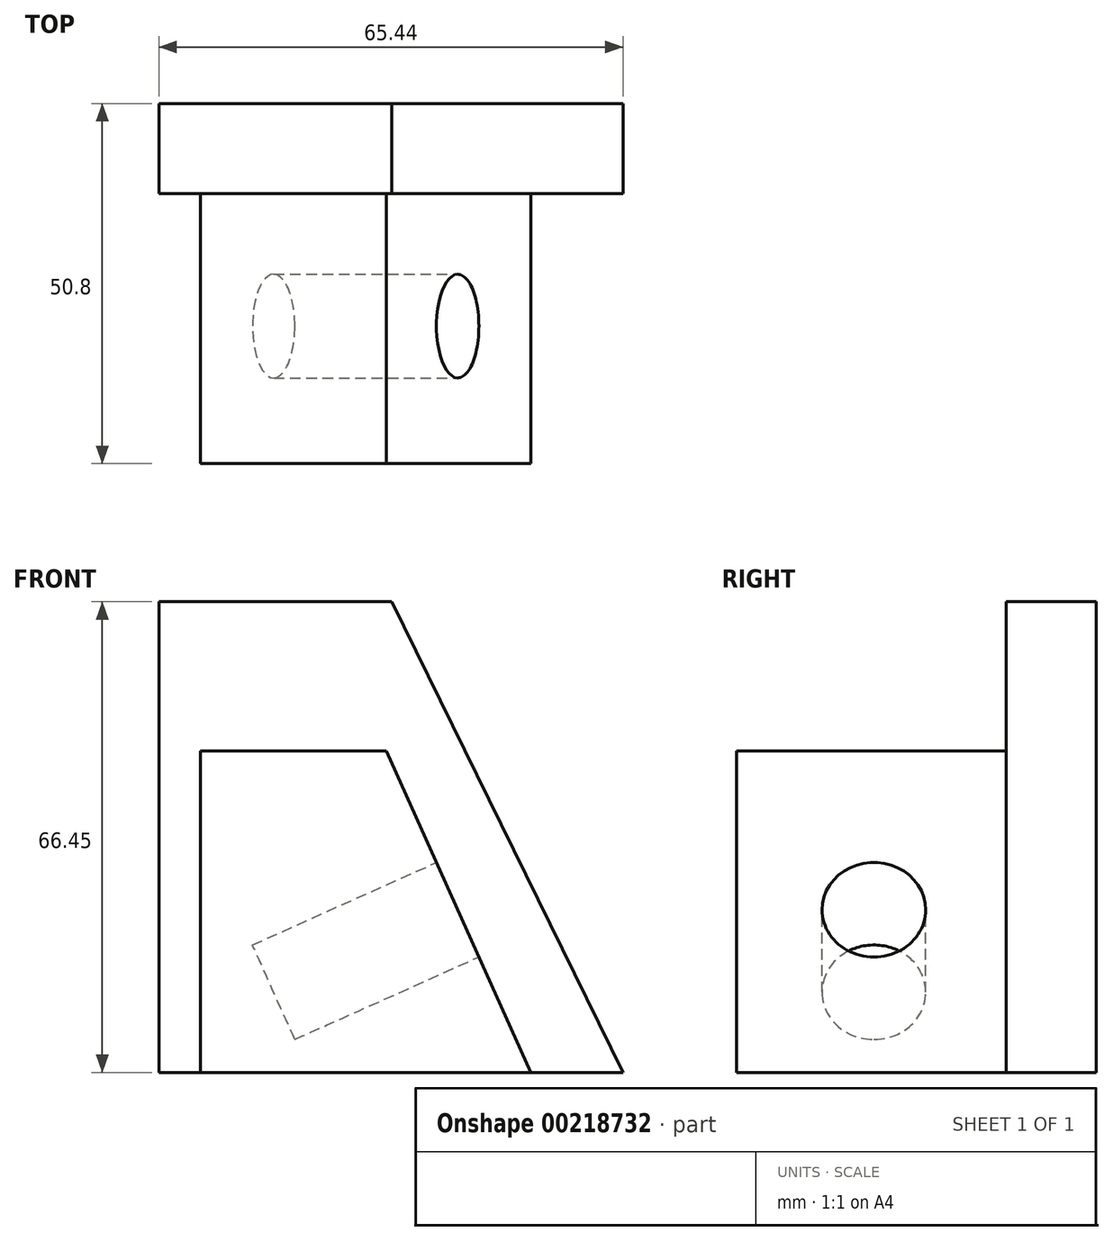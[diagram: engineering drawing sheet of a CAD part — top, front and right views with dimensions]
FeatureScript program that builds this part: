
annotation { "Feature Type Name" : "Feature", "Feature Type Description" : "" }
export const myFeature = defineFeature(function(context is Context, id is Id, definition is map)
    precondition{}
    {
        {
            var Q0;
            Q0=qCreatedBy(makeId("Front.planeOp"),FACE);
            var sketch = newSketch(context, id + "F0", { "sketchPlane" : qUnion([Q0])});
            skLineSegment(sketch, "E0", {"start": v(0, 0) * mm, "end": v(-32.63, 66.45) * mm});
            skLineSegment(sketch, "E1", {"start": v(-32.63, 66.45) * mm, "end": v(-65.44, 66.45) * mm});
            skLineSegment(sketch, "E2", {"start": v(-65.44, 66.45) * mm, "end": v(-65.44, 0) * mm});
            skLineSegment(sketch, "E3", {"start": v(-65.44, 0) * mm, "end": v(0, 0) * mm});
            skSolve(sketch);
        }
        {
            var Q0;
            Q0=makeQuery(id+"F0.imprint","IMPRINT",FACE,{"disambiguationData":[TD([[makeQuery(id+"F0.imprint","IMPRINT",EDGE,{"derivedFrom":sQuery(id+"F0.wireOp",EDGE,"E0")}),1.0]])]});
            extrude(context, id + "F1", {"entities" : qUnion([Q0]), "depth" : 12.7 * mm});
        }
        {
            var Q0;
            Q0=makeQuery(id+"F1.opExtrude","CAP_FACE",FACE,{"disambiguationData":[OSD([sQuery(id+"F0.wireOp",EDGE,"E0"),sQuery(id+"F0.wireOp",EDGE,"E1"),sQuery(id+"F0.wireOp",EDGE,"E2"),sQuery(id+"F0.wireOp",EDGE,"E3")])],"isStart":false});
            var sketch = newSketch(context, id + "F2", { "sketchPlane" : qUnion([Q0])});
            skLineSegment(sketch, "E4", {"start": v(-13.01, 0) * mm, "end": v(-33.36, 45.37) * mm});
            skLineSegment(sketch, "E5", {"start": v(-33.36, 45.37) * mm, "end": v(-59.57, 45.37) * mm});
            skLineSegment(sketch, "E6", {"start": v(-59.57, 45.37) * mm, "end": v(-59.57, 0) * mm});
            skLineSegment(sketch, "E7", {"start": v(-59.57, 0) * mm, "end": v(-13.01, 0) * mm});
            skSolve(sketch);
        }
        {
            var Q0;
            Q0=makeQuery(id+"F2.imprint","IMPRINT",FACE,{"disambiguationData":[TD([[makeQuery(id+"F2.imprint","IMPRINT",EDGE,{"derivedFrom":sQuery(id+"F2.wireOp",EDGE,"E4")}),1.0]])]});
            extrude(context, id + "F3", {"entities" : qUnion([Q0]), "operationType" : NewBodyOperationType.ADD, "depth" : 25.4 * mm});
        }
        {
            var Q0;
            Q0=makeQuery(id+"F3.opExtrude","CAP_FACE",FACE,{"disambiguationData":[OSD([sQuery(id+"F2.wireOp",EDGE,"E4"),sQuery(id+"F2.wireOp",EDGE,"E5"),sQuery(id+"F2.wireOp",EDGE,"E6"),sQuery(id+"F2.wireOp",EDGE,"E7")])],"isStart":false});
            extrude(context, id + "F4", {"entities" : qUnion([Q0]), "operationType" : NewBodyOperationType.ADD, "depth" : 12.7 * mm});
        }
        {
            var Q0;
            {var subQ0=sQuery(id+"F2.wireOp",EDGE,"E4");Q0=makeQuery(id+"F4.boolean.opBoolean","MERGE",FACE,{"derivedFrom":[makeQuery(id+"F3.opExtrude","SWEPT_FACE",FACE,{"disambiguationData":[OSD([subQ0])]}),makeQuery(id+"F4.opExtrude","SWEPT_FACE",FACE,{"disambiguationData":[OSD([subQ0])]})]});}
            var sketch = newSketch(context, id + "F5", { "sketchPlane" : qUnion([Q0])});
            skCircle(sketch, "E8", {"center": v(-31.4, 30.5) * mm, "radius": 7.31 * mm});
            skSolve(sketch);
        }
        {
            var Q0;
            Q0=makeQuery(id+"F5.imprint","IMPRINT",FACE,{"disambiguationData":[TD([[makeQuery(id+"F5.imprint","IMPRINT",EDGE,{"derivedFrom":sQuery(id+"F5.wireOp",EDGE,"E8")}),1.0]])]});
            extrude(context, id + "F6", {"entities" : qUnion([Q0]), "operationType" : NewBodyOperationType.REMOVE, "oppositeDirection" : true, "depth" : 28.45 * mm});
        }
    });
